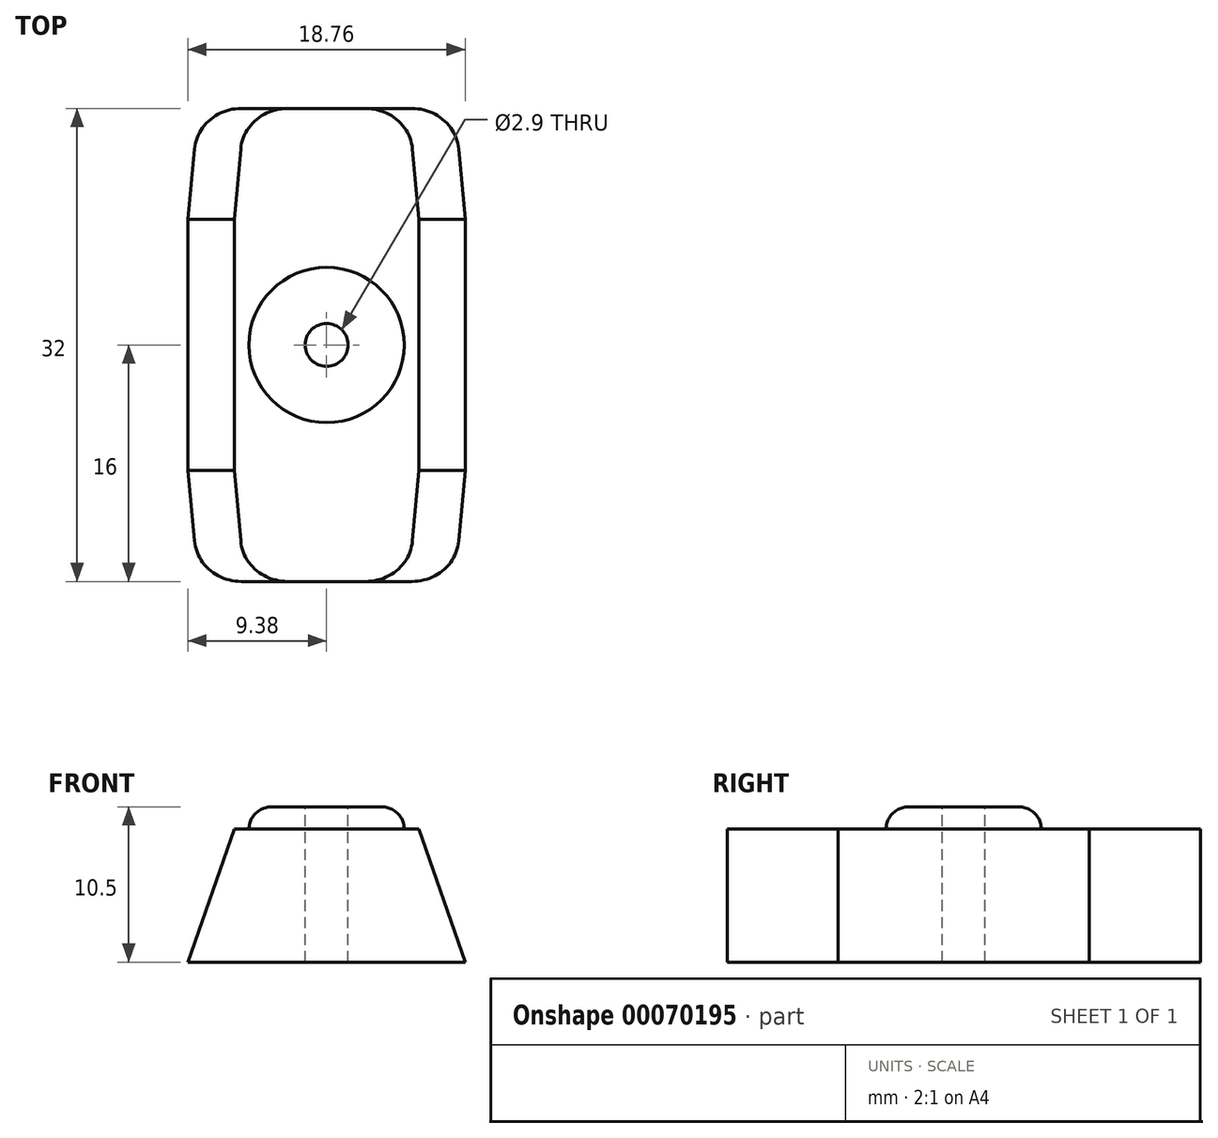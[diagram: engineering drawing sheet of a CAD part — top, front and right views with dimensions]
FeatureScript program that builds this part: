
annotation { "Feature Type Name" : "Feature", "Feature Type Description" : "" }
export const myFeature = defineFeature(function(context is Context, id is Id, definition is map)
    precondition{}
    {
        {
            var Q0;
            Q0=qCreatedBy(makeId("Front.planeOp"),FACE);
            var sketch = newSketch(context, id + "F0", { "sketchPlane" : qUnion([Q0])});
            skLineSegment(sketch, "E0", {"start": v(0, 0) * mm, "end": v(6.25, 0) * mm});
            skLineSegment(sketch, "E1", {"start": v(6.25, 0) * mm, "end": v(9.38, -9) * mm});
            skLineSegment(sketch, "E2", {"start": v(9.38, -9) * mm, "end": v(0, -9) * mm});
            skLineSegment(sketch, "E3.MirrorCS", {"start": v(-9.38, -9) * mm, "end": v(0, -9) * mm});
            skLineSegment(sketch, "E4.MirrorCS", {"start": v(0, 0) * mm, "end": v(-6.25, 0) * mm});
            skLineSegment(sketch, "E5.MirrorCS", {"start": v(-6.25, 0) * mm, "end": v(-9.37, -9) * mm});
            skSolve(sketch);
        }
        {
            var Q0;
            Q0=makeQuery(id+"F0.imprint","IMPRINT",FACE,{"disambiguationData":[TD([[makeQuery(id+"F0.imprint","IMPRINT",EDGE,{"derivedFrom":sQuery(id+"F0.wireOp",EDGE,"E0")}),-1.0]])]});
            extrude(context, id + "F1", {"entities" : qUnion([Q0]), "endBound" : BoundingType.SYMMETRIC, "depth" : 32 * mm});
        }
        {
            var Q0;
            Q0=makeQuery(id+"F1.opExtrude","SWEPT_FACE",FACE,{"disambiguationData":[OSD([sQuery(id+"F0.wireOp",EDGE,"E0"),sQuery(id+"F0.wireOp",EDGE,"E4.MirrorCS")])]});
            var sketch = newSketch(context, id + "F2", { "sketchPlane" : qUnion([Q0])});
            skCircle(sketch, "E6", {"center": v(0, 0) * mm, "radius": 5.25 * mm});
            skSolve(sketch);
        }
        {
            var Q0;
            Q0=makeQuery(id+"F2.imprint","IMPRINT",FACE,{"disambiguationData":[TD([[makeQuery(id+"F2.imprint","IMPRINT",EDGE,{"derivedFrom":sQuery(id+"F2.wireOp",EDGE,"E6")}),1.0]])]});
            extrude(context, id + "F3", {"entities" : qUnion([Q0]), "operationType" : NewBodyOperationType.ADD, "depth" : 1.5 * mm});
        }
        {
            var Q0;
            Q0=makeQuery(id+"F3.opExtrude","CAP_FACE",FACE,{"disambiguationData":[OSD([sQuery(id+"F2.wireOp",EDGE,"E6")])],"isStart":false});
            var sketch = newSketch(context, id + "F4", { "sketchPlane" : qUnion([Q0])});
            skCircle(sketch, "E7", {"center": v(0, 0) * mm, "radius": 1.45 * mm});
            skSolve(sketch);
        }
        {
            var Q0;
            Q0=makeQuery(id+"F4.imprint","IMPRINT",FACE,{"disambiguationData":[TD([[makeQuery(id+"F4.imprint","IMPRINT",EDGE,{"derivedFrom":sQuery(id+"F4.wireOp",EDGE,"E7")}),1.0]])]});
            extrude(context, id + "F5", {"entities" : qUnion([Q0]), "operationType" : NewBodyOperationType.REMOVE, "oppositeDirection" : true, "depth" : 12 * mm});
        }
        {
            var Q0;
            Q0=makeQuery(id+"F1.opExtrude","CAP_EDGE",EDGE,{"disambiguationData":[OSD([sQuery(id+"F0.wireOp",EDGE,"E1")])],"isStart":false});
            var Q1;
            Q1=makeQuery(id+"F1.opExtrude","CAP_EDGE",EDGE,{"disambiguationData":[OSD([sQuery(id+"F0.wireOp",EDGE,"E5.MirrorCS")])],"isStart":false});
            var Q2;
            Q2=makeQuery(id+"F1.opExtrude","CAP_EDGE",EDGE,{"disambiguationData":[OSD([sQuery(id+"F0.wireOp",EDGE,"E1")])],"isStart":true});
            var Q3;
            Q3=makeQuery(id+"F1.opExtrude","CAP_EDGE",EDGE,{"disambiguationData":[OSD([sQuery(id+"F0.wireOp",EDGE,"E5.MirrorCS")])],"isStart":true});
            chamfer(context, id + "F6", {"entities" : qUnion([Q0, Q1, Q2, Q3]), "chamferType" : ChamferType.OFFSET_ANGLE, "width" : 7.5 * mm, "oppositeDirection" : false, "angle" : 5 * degree, "tangentPropagation" : true});
        }
        {
            var Q0;
            {var subQ0=sQuery(id+"F0.wireOp",EDGE,"E1");Q0=makeQuery(id+"F6.opChamfer","BLEND_EDGE",EDGE,{"blendedFrom":[makeQuery(id+"F1.opExtrude","CAP_EDGE",EDGE,{"disambiguationData":[OSD([subQ0])],"isStart":false}),makeQuery(id+"F1.opExtrude","CAP_FACE",FACE,{"disambiguationData":[OSD([sQuery(id+"F0.wireOp",EDGE,"E0"),subQ0,sQuery(id+"F0.wireOp",EDGE,"E2"),sQuery(id+"F0.wireOp",EDGE,"E3.MirrorCS"),sQuery(id+"F0.wireOp",EDGE,"E4.MirrorCS"),sQuery(id+"F0.wireOp",EDGE,"E5.MirrorCS")])],"isStart":false})],"blendedInto":[makeQuery(id+"F1.opExtrude","CAP_FACE",FACE,{"disambiguationData":[OSD([sQuery(id+"F0.wireOp",EDGE,"E0"),subQ0,sQuery(id+"F0.wireOp",EDGE,"E2"),sQuery(id+"F0.wireOp",EDGE,"E3.MirrorCS"),sQuery(id+"F0.wireOp",EDGE,"E4.MirrorCS"),sQuery(id+"F0.wireOp",EDGE,"E5.MirrorCS")])],"isStart":false})]});}
            var Q1;
            {var subQ0=sQuery(id+"F0.wireOp",EDGE,"E5.MirrorCS");Q1=makeQuery(id+"F6.opChamfer","BLEND_EDGE",EDGE,{"blendedFrom":[makeQuery(id+"F1.opExtrude","CAP_EDGE",EDGE,{"disambiguationData":[OSD([subQ0])],"isStart":false}),makeQuery(id+"F1.opExtrude","CAP_FACE",FACE,{"disambiguationData":[OSD([sQuery(id+"F0.wireOp",EDGE,"E0"),sQuery(id+"F0.wireOp",EDGE,"E1"),sQuery(id+"F0.wireOp",EDGE,"E2"),sQuery(id+"F0.wireOp",EDGE,"E3.MirrorCS"),sQuery(id+"F0.wireOp",EDGE,"E4.MirrorCS"),subQ0])],"isStart":false})],"blendedInto":[makeQuery(id+"F1.opExtrude","CAP_FACE",FACE,{"disambiguationData":[OSD([sQuery(id+"F0.wireOp",EDGE,"E0"),sQuery(id+"F0.wireOp",EDGE,"E1"),sQuery(id+"F0.wireOp",EDGE,"E2"),sQuery(id+"F0.wireOp",EDGE,"E3.MirrorCS"),sQuery(id+"F0.wireOp",EDGE,"E4.MirrorCS"),subQ0])],"isStart":false})]});}
            var Q2;
            {var subQ0=sQuery(id+"F0.wireOp",EDGE,"E1");Q2=makeQuery(id+"F6.opChamfer","BLEND_EDGE",EDGE,{"blendedFrom":[makeQuery(id+"F1.opExtrude","CAP_EDGE",EDGE,{"disambiguationData":[OSD([subQ0])],"isStart":true}),makeQuery(id+"F1.opExtrude","CAP_FACE",FACE,{"disambiguationData":[OSD([sQuery(id+"F0.wireOp",EDGE,"E0"),subQ0,sQuery(id+"F0.wireOp",EDGE,"E2"),sQuery(id+"F0.wireOp",EDGE,"E3.MirrorCS"),sQuery(id+"F0.wireOp",EDGE,"E4.MirrorCS"),sQuery(id+"F0.wireOp",EDGE,"E5.MirrorCS")])],"isStart":true})],"blendedInto":[makeQuery(id+"F1.opExtrude","CAP_FACE",FACE,{"disambiguationData":[OSD([sQuery(id+"F0.wireOp",EDGE,"E0"),subQ0,sQuery(id+"F0.wireOp",EDGE,"E2"),sQuery(id+"F0.wireOp",EDGE,"E3.MirrorCS"),sQuery(id+"F0.wireOp",EDGE,"E4.MirrorCS"),sQuery(id+"F0.wireOp",EDGE,"E5.MirrorCS")])],"isStart":true})]});}
            var Q3;
            {var subQ0=sQuery(id+"F0.wireOp",EDGE,"E5.MirrorCS");Q3=makeQuery(id+"F6.opChamfer","BLEND_EDGE",EDGE,{"blendedFrom":[makeQuery(id+"F1.opExtrude","CAP_EDGE",EDGE,{"disambiguationData":[OSD([subQ0])],"isStart":true}),makeQuery(id+"F1.opExtrude","CAP_FACE",FACE,{"disambiguationData":[OSD([sQuery(id+"F0.wireOp",EDGE,"E0"),sQuery(id+"F0.wireOp",EDGE,"E1"),sQuery(id+"F0.wireOp",EDGE,"E2"),sQuery(id+"F0.wireOp",EDGE,"E3.MirrorCS"),sQuery(id+"F0.wireOp",EDGE,"E4.MirrorCS"),subQ0])],"isStart":true})],"blendedInto":[makeQuery(id+"F1.opExtrude","CAP_FACE",FACE,{"disambiguationData":[OSD([sQuery(id+"F0.wireOp",EDGE,"E0"),sQuery(id+"F0.wireOp",EDGE,"E1"),sQuery(id+"F0.wireOp",EDGE,"E2"),sQuery(id+"F0.wireOp",EDGE,"E3.MirrorCS"),sQuery(id+"F0.wireOp",EDGE,"E4.MirrorCS"),subQ0])],"isStart":true})]});}
            fillet(context, id + "F7", {"entities" : qUnion([Q0, Q1, Q2, Q3]), "radius" : 3 * mm, "tangentPropagation" : true, "allowEdgeOverflow" : false});
        }
        {
            var Q0;
            Q0=makeQuery(id+"F3.opExtrude","CAP_EDGE",EDGE,{"disambiguationData":[OSD([sQuery(id+"F2.wireOp",EDGE,"E6")])],"isStart":false});
            fillet(context, id + "F8", {"entities" : qUnion([Q0]), "radius" : 1.5 * mm, "tangentPropagation" : true, "allowEdgeOverflow" : false});
        }
    });
